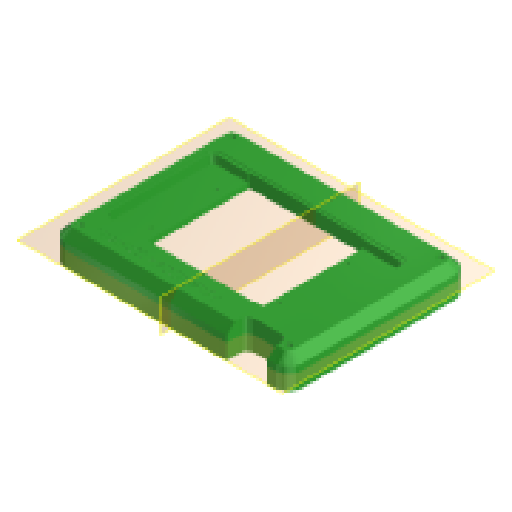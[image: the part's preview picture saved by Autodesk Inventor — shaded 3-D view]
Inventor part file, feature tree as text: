
AUTODESK INVENTOR PART (.ipt)
format: ipt  version: 2024.1 (Build 281209000, 209)  size: 911,872 bytes
history: native  units: mm
features: sketch x9, extrude x8, reference x8, projected_geometry x8, plane x5, other x4, chamfer x1, hole x1
ambient origin geometry x8: Origin, YZ Plane, XZ Plane, XY Plane, X Axis, Y Axis, Z Axis, Center Point
bodies: Volumenkörper1 (feature_tree)
feature tree (44):
  plane  "Arbeitsebene1"
  plane  "Arbeitsebene2"
  extrude  "Extrusion1"  Depth=10.0mm
  plane  "Arbeitsebene3"
  extrude  "Extrusion2"  Depth=10.0mm TaperAngle=0.0deg
  sketch  "Skizze3"  dims[d10=10.0mm d11=0.0mm d12=8.0mm d13=2.0mm d14=45.0deg]
  plane  "Arbeitsebene4"
  extrude  "Extrusion3"  Depth=8.0mm TaperAngle=45.0deg
  chamfer  "Fasen1"  [1 undecoded]
  extrude  "Extrusion4"  Depth=15.0mm TaperAngle=0.0deg
  extrude  "Extrusion5"  Depth=14.0mm
  extrude  "Extrusion6"  Depth=14.0mm
  hole  "Bohrung1"  [1 undecoded]
  extrude  "Extrusion7"  Depth=14.0mm
  extrude  "Extrusion8"  Depth=14.0mm
  plane  "Arbeitsebene5"
  sketch  "Skizze1"  dims[d2=1.0mm d3=0.0mm d4=10.0mm]
  reference  "Referenz2"
  reference  "Referenz3"
  reference  "Referenz4"
  reference  "Referenz5"
  reference  "Referenz6"
  sketch  "Skizze2"  dims[d5=5.0mm d7=10.0mm d8=0.0mm]
  sketch  "Skizze4"  dims[d15=40.0mm]
  reference  "Referenz9"
  projected_geometry  "Projizierte Kontur3"
  sketch  "Skizze5"  dims[d16=20.0mm]
  projected_geometry  "Projizierte Kontur4"
  sketch  "Skizze6"  dims[d17=7.0mm]
  projected_geometry  "Projizierte Kontur5"
  sketch  "Skizze7"  dims[d18=20.0mm d19=0.0mm d20=0.0mm]
  reference  "Referenz10"
  projected_geometry  "Projizierte Kontur6"
  sketch  "Skizze8"  dims[d21=6.0mm d22=15.0mm d23=0.0mm]
  projected_geometry  "Projizierte Kontur7"
  projected_geometry  "Projizierte Kontur8"
  sketch  "Skizze9"  dims[d24=0.5mm d25=0.0mm d26=3.3mm d27=6.0mm d28=6.5mm d29=3.5mm d30=90.0deg d31=15.0mm d32=20.594885mm d33=14.0mm d34=14.0mm d35=14.0mm d36=14.0mm d37=14.0mm d38=14.0mm d39=14.0mm d40=14.0mm d41=0.5mm d42=0.0mm d43=5.0mm d44=135.0deg d45=135.0deg d46=45.0mm d47=45.0deg d48=45.0deg d49=5.0mm d50=45.0deg d51=5.0mm d52=5.0mm d53=135.0deg d54=5.0mm d56=5.0mm d57=5.0mm d58=5.0mm d59=6.5mm d62=6.5mm d63=6.5mm d64=5.0mm d65=5.0mm d66=6.5mm d67=6.5mm d68=10.0mm d69=-3.490659mm d70=1.0mm d71=1.0mm d72=1.0mm d73=1.0mm d74=3.0mm d75=3.0mm d76=3.0mm d77=0.5mm]
  reference  "Referenz11"
  projected_geometry  "Projizierte Kontur9"
  projected_geometry  "Projizierte Kontur10"
  other  "Assembly_Planktoscope_Lid_Screen.iam"
  other  "00_raspberry pi display:1"
  other  "00_OutdoorCase_Type2000_toplid:1"
  other  "Baugruppe2"
note: 2 required parameter values undecoded (feature->parameter linkage not recoverable at this tier; creation-order binding heuristic only, values carry confidence <= 0.55)
